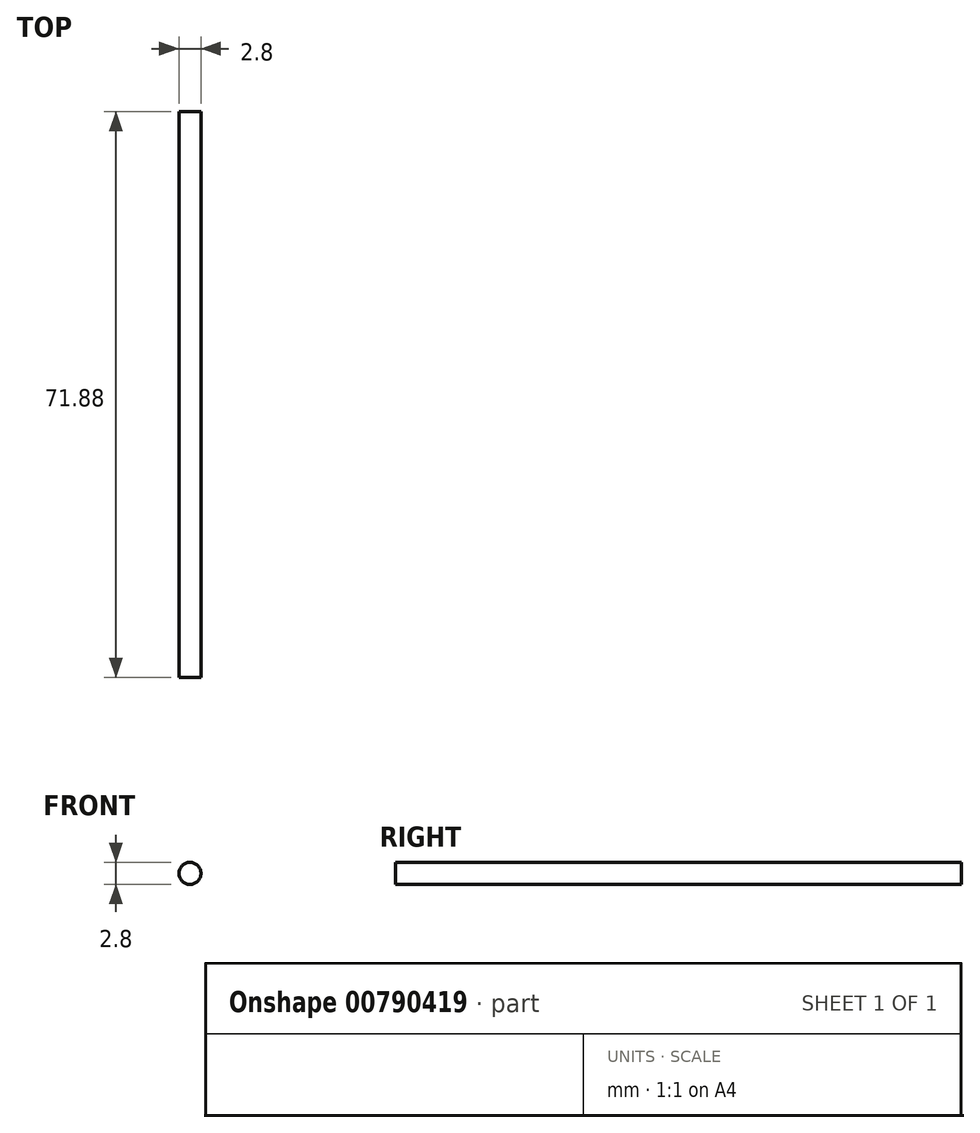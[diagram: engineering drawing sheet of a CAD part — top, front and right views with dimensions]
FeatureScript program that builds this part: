
annotation { "Feature Type Name" : "Feature", "Feature Type Description" : "" }
export const myFeature = defineFeature(function(context is Context, id is Id, definition is map)
    precondition{}
    {
        {
            var Q0;
            Q0=qCreatedBy(makeId("Front.planeOp"),FACE);
            var sketch = newSketch(context, id + "F0", { "sketchPlane" : qUnion([Q0])});
            skCircle(sketch, "E0", {"center": v(0, 0) * mm, "radius": 1.4 * mm});
            skSolve(sketch);
        }
        {
            var Q0;
            Q0=makeQuery(id+"F0.imprint","IMPRINT",FACE,{"disambiguationData":[TD([[makeQuery(id+"F0.imprint","IMPRINT",EDGE,{"derivedFrom":sQuery(id+"F0.wireOp",EDGE,"E0")}),1.0]])]});
            extrude(context, id + "F1", {"entities" : qUnion([Q0]), "depth" : 71.88 * mm, "offsetDistance" : 25.4 * mm});
        }
    });
